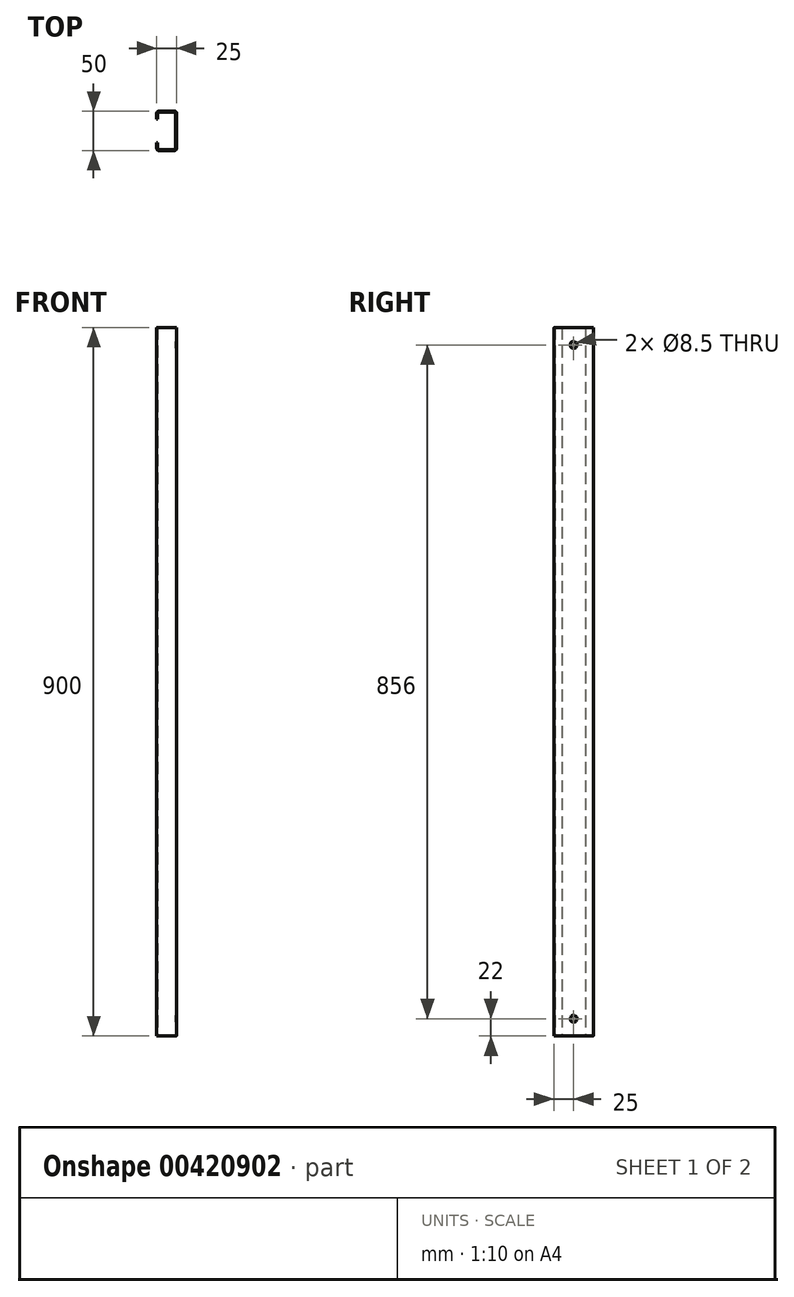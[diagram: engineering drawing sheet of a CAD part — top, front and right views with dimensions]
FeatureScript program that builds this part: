
annotation { "Feature Type Name" : "Feature", "Feature Type Description" : "" }
export const myFeature = defineFeature(function(context is Context, id is Id, definition is map)
    precondition{}
    {
        {
            var Q0;
            Q0=qCreatedBy(makeId("Top.planeOp"),FACE);
            var sketch = newSketch(context, id + "F0", { "sketchPlane" : qUnion([Q0])});
            skLineSegment(sketch, "E0", {"start": v(10, 25) * mm, "end": v(-10, 25) * mm});
            skArc(sketch, "E1", {"start": v(-10, 25) * mm, "mid": v(-11.77, 24.27) * mm, "end": v(-12.5, 22.5) * mm});
            skLineSegment(sketch, "E2", {"start": v(-12.5, 22.5) * mm, "end": v(-12.5, 15) * mm});
            skLineSegment(sketch, "E3", {"start": v(-12.5, 15) * mm, "end": v(-11.3, 15) * mm});
            skLineSegment(sketch, "E4", {"start": v(-11.3, 15) * mm, "end": v(-11.3, 22.5) * mm});
            skArc(sketch, "E5", {"start": v(-11.3, 22.5) * mm, "mid": v(-10.92, 23.42) * mm, "end": v(-10, 23.8) * mm});
            skLineSegment(sketch, "E6", {"start": v(-10, 23.8) * mm, "end": v(10, 23.8) * mm});
            skArc(sketch, "E7", {"start": v(10, 23.8) * mm, "mid": v(10.92, 23.42) * mm, "end": v(11.3, 22.5) * mm});
            skLineSegment(sketch, "E8", {"start": v(11.3, 22.5) * mm, "end": v(11.3, -22.5) * mm});
            skArc(sketch, "E9", {"start": v(11.3, -22.5) * mm, "mid": v(10.92, -23.42) * mm, "end": v(10, -23.8) * mm});
            skLineSegment(sketch, "E10", {"start": v(10, -23.8) * mm, "end": v(-10, -23.8) * mm});
            skArc(sketch, "E11", {"start": v(-10, -23.8) * mm, "mid": v(-10.92, -23.42) * mm, "end": v(-11.3, -22.5) * mm});
            skLineSegment(sketch, "E12", {"start": v(-11.3, -22.5) * mm, "end": v(-11.3, -15) * mm});
            skLineSegment(sketch, "E13", {"start": v(-11.3, -15) * mm, "end": v(-12.5, -15) * mm});
            skLineSegment(sketch, "E14", {"start": v(-12.5, -15) * mm, "end": v(-12.5, -22.5) * mm});
            skArc(sketch, "E15", {"start": v(-12.5, -22.5) * mm, "mid": v(-11.77, -24.27) * mm, "end": v(-10, -25) * mm});
            skLineSegment(sketch, "E16", {"start": v(-10, -25) * mm, "end": v(10, -25) * mm});
            skArc(sketch, "E17", {"start": v(10, -25) * mm, "mid": v(11.77, -24.27) * mm, "end": v(12.5, -22.5) * mm});
            skLineSegment(sketch, "E18", {"start": v(12.5, -22.5) * mm, "end": v(12.5, 22.5) * mm});
            skArc(sketch, "E19", {"start": v(12.5, 22.5) * mm, "mid": v(11.77, 24.27) * mm, "end": v(10, 25) * mm});
            skSolve(sketch);
        }
        {
            assignVariable(context, id + "F1", {"name" : "Longitud", "anyValue" : 900});
        }
        {
            var Q0;
            Q0 = qSketchRegion(id + "F0", true);
            extrude(context, id + "F2", {"entities" : qUnion([Q0]), "depth" : (getVariable(context, 'Longitud')) * mm});
        }
        {
            var Q0;
            Q0=makeQuery(id+"F2.opExtrude","SWEPT_FACE",FACE,{"disambiguationData":[OSD([sQuery(id+"F0.wireOp",EDGE,"E18")])]});
            var sketch = newSketch(context, id + "F3", { "sketchPlane" : qUnion([Q0])});
            skCircle(sketch, "E20", {"center": v(0, 22) * mm, "radius": 4.25 * mm});
            skCircle(sketch, "E21", {"center": v(0, 878) * mm, "radius": 4.25 * mm});
            skSolve(sketch);
        }
        {
            var Q0;
            Q0 = qSketchRegion(id + "F3", true);
            var Q1;
            Q1=makeQuery(id+"F2.opExtrude","SWEPT_FACE",FACE,{"disambiguationData":[OSD([sQuery(id+"F0.wireOp",EDGE,"E8")])]});
            extrude(context, id + "F4", {"entities" : qUnion([Q0]), "operationType" : NewBodyOperationType.REMOVE, "endBound" : BoundingType.UP_TO_SURFACE, "oppositeDirection" : true, "endBoundEntityFace" : qUnion([Q1]), "depth" : 25 * mm});
        }
    });
